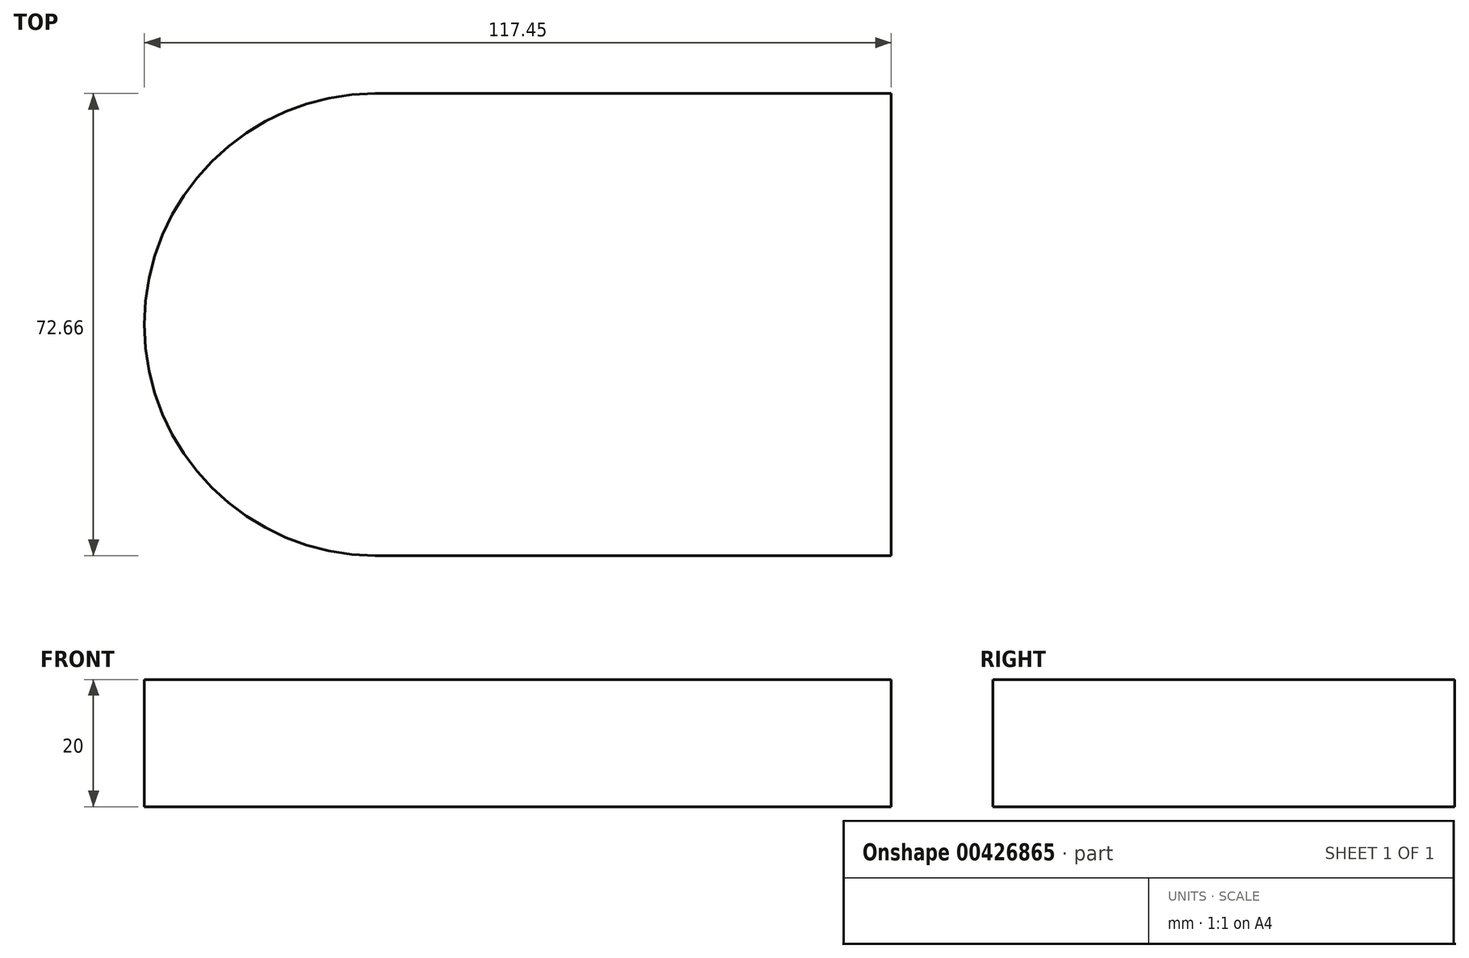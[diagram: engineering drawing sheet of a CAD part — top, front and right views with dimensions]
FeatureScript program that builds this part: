
annotation { "Feature Type Name" : "Feature", "Feature Type Description" : "" }
export const myFeature = defineFeature(function(context is Context, id is Id, definition is map)
    precondition{}
    {
        {
            var Q0;
            Q0=qCreatedBy(makeId("Top.planeOp"),FACE);
            var sketch = newSketch(context, id + "F0", { "sketchPlane" : qUnion([Q0])});
            skLineSegment(sketch, "E0.bottom", {"start": v(-40.56, 36.33) * mm, "end": v(40.56, 36.33) * mm});
            skLineSegment(sketch, "E0.top", {"start": v(-40.56, -36.33) * mm, "end": v(40.56, -36.33) * mm});
            skLineSegment(sketch, "E0.left", {"start": v(-40.56, 36.33) * mm, "end": v(-40.56, -36.33) * mm});
            skLineSegment(sketch, "E0.right", {"start": v(40.56, 36.33) * mm, "end": v(40.56, -36.33) * mm});
            skPoint(sketch, "E0.middle", {"position": v(0, 0) * mm});
            skCircle(sketch, "E1", {"center": v(-40.56, 0) * mm, "radius": 36.33 * mm});
            skSolve(sketch);
        }
        {
            var Q0;
            Q0 = qSketchRegion(id + "F0", true);
            extrude(context, id + "F1", {"entities" : qUnion([Q0]), "depth" : 20 * mm, "offsetDistance" : 25 * mm});
        }
    });
